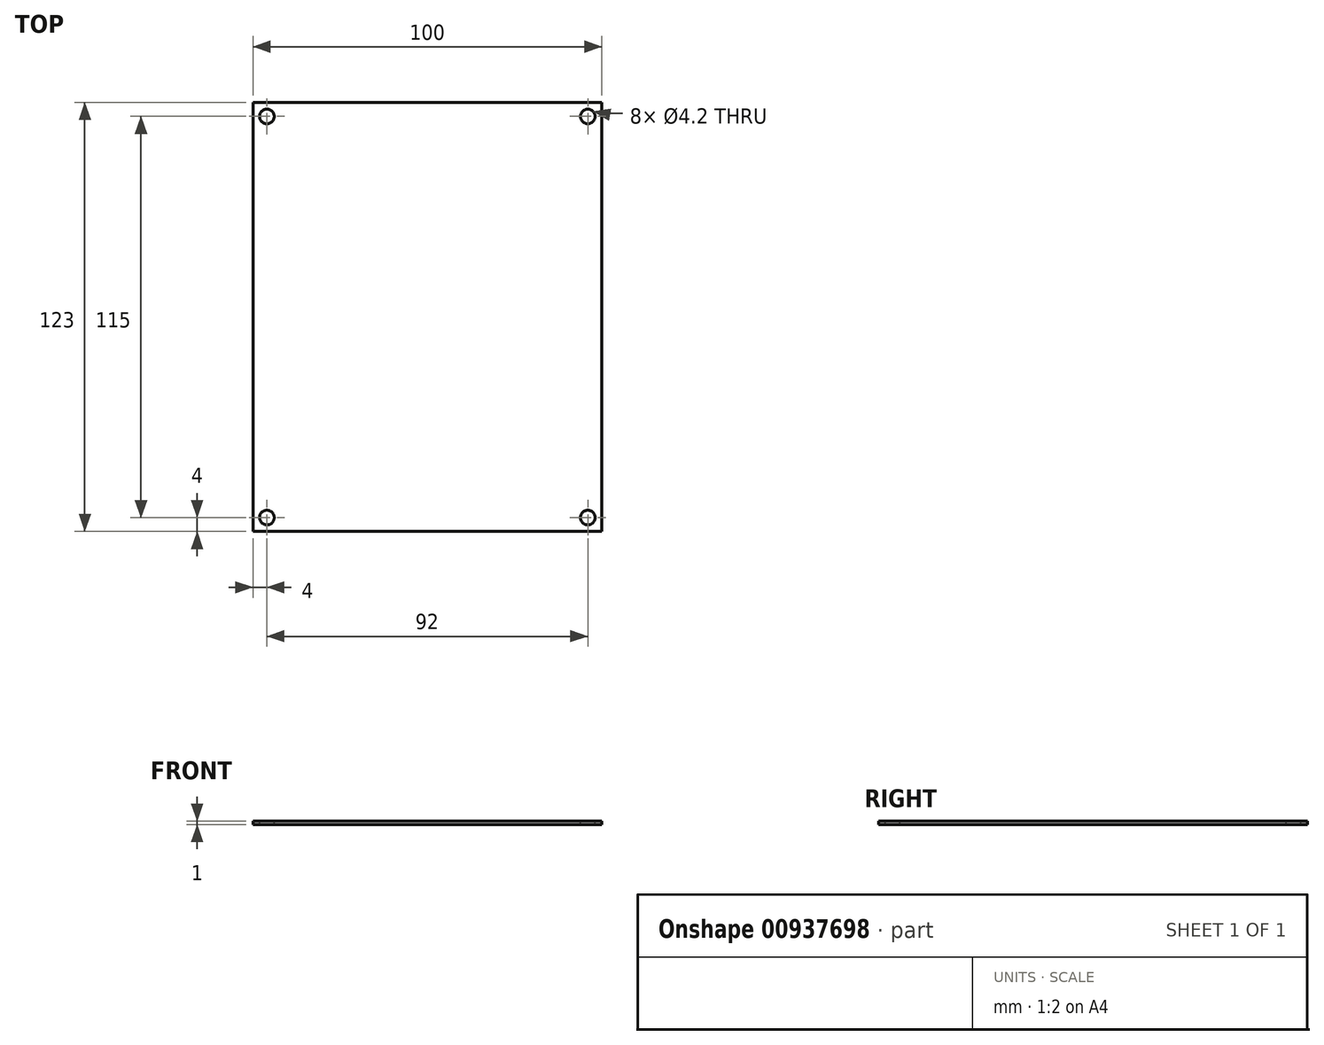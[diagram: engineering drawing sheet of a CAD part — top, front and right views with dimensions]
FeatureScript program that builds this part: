
annotation { "Feature Type Name" : "Feature", "Feature Type Description" : "" }
export const myFeature = defineFeature(function(context is Context, id is Id, definition is map)
    precondition{}
    {
        {
            var Q0;
            Q0=qCreatedBy(makeId("Top.planeOp"),FACE);
            var sketch = newSketch(context, id + "F0", { "sketchPlane" : qUnion([Q0])});
            skLineSegment(sketch, "E0.bottom", {"start": v(-50, 61.5) * mm, "end": v(50, 61.5) * mm});
            skLineSegment(sketch, "E0.top", {"start": v(-50, -61.5) * mm, "end": v(50, -61.5) * mm});
            skLineSegment(sketch, "E0.left", {"start": v(-50, 61.5) * mm, "end": v(-50, -61.5) * mm});
            skLineSegment(sketch, "E0.right", {"start": v(50, 61.5) * mm, "end": v(50, -61.5) * mm});
            skLineSegment(sketch, "E1.bottom", {"start": v(-46, 57.5) * mm, "end": v(46, 57.5) * mm, "construction": true});
            skLineSegment(sketch, "E1.top", {"start": v(-46, -57.5) * mm, "end": v(46, -57.5) * mm, "construction": true});
            skLineSegment(sketch, "E1.left", {"start": v(-46, 57.5) * mm, "end": v(-46, -57.5) * mm, "construction": true});
            skLineSegment(sketch, "E1.right", {"start": v(46, 57.5) * mm, "end": v(46, -57.5) * mm, "construction": true});
            skSolve(sketch);
        }
        {
            var Q0;
            Q0=makeQuery(id+"F0.imprint","IMPRINT",FACE,{"disambiguationData":[TD([[makeQuery(id+"F0.imprint","IMPRINT",EDGE,{"derivedFrom":sQuery(id+"F0.wireOp",EDGE,"E0.bottom")}),-1.0]])]});
            extrude(context, id + "F1", {"entities" : qUnion([Q0]), "oppositeDirection" : true, "depth" : 1 * mm, "offsetDistance" : 25 * mm});
        }
        {
            var Q0;
            Q0=sQuery(id+"F0.wireOp",VERTEX,"E1.bottom.start");
            var Q1;
            Q1=sQuery(id+"F0.wireOp",VERTEX,"E1.top.start");
            var Q2;
            Q2=sQuery(id+"F0.wireOp",VERTEX,"E1.top.end");
            var Q3;
            Q3=sQuery(id+"F0.wireOp",VERTEX,"E1.bottom.end");
            var Q4;
            Q4=makeQuery(id+"F1.opExtrude","SWEPT_BODY",BODY,{"disambiguationData":[OSD([sQuery(id+"F0.wireOp",EDGE,"E0.bottom"),sQuery(id+"F0.wireOp",EDGE,"E0.top"),sQuery(id+"F0.wireOp",EDGE,"E0.left"),sQuery(id+"F0.wireOp",EDGE,"E0.right")])]});
            hole(context, id + "F2", {"style" : HoleStyle.SIMPLE, "endStyle" : HoleEndStyle.BLIND, "holeDiameter" : 4.2 * mm, "majorDiameter" : 5 * mm, "holeDepth" : 7 * mm, "isTappedThrough" : true, "tappedDepth" : 20 * mm, "tapClearance" : 3, "locations" : qUnion([Q0, Q1, Q2, Q3]), "scope" : qUnion([Q4])});
        }
    });
